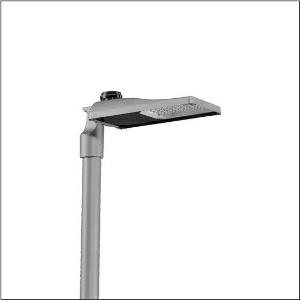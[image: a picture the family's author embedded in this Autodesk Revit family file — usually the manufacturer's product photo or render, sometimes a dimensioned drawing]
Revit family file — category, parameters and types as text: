
# Revit family: streetlight_sl_31_mini___st1_0a_5xh6d35n08ha_c5a6
name_source: partatom
category: Lighting Fixtures
units: mm (PartAtom-declared; Revit-internal decimal feet)

## family parameters
Cut with Voids When Loaded = No
Host = Face
Light Source = No
Part Type = Normal
Room Calculation Point = No
Round Connector Dimension = Use Diameter
Shared = No

## types (1)
- --- (1 x LED, 9240 lm, 68.3 W, 3000K)
    Apparent Load = 68 VA
    CIE Flux Codes = 37 72 97 100 100
    Color Rendering = 70
    Color Temperature = 3000K
    Default Elevation = 1800 mm
    Description = Streetlight SL 31 mini NEMA (7pin), Desk-Remote mast luminaire for post-top, side-entry; light control with lens of PMMA; light distribution: ST1.0a, direct asymmetric distribution, for standard-compliant lighting for roads and squares; LED: luminous flux: 9.240lm, light colour: 730, colour temperature: 3000K; luminous efficacy: 135,3lm/W; control: pre-setting: linear dimming characteristic, flexible luminous flux parameterisation, time-dependent luminous flux control, constant luminous flux control, intelligent temperature release in ECG and LED module, overheat protection; luminaire housing, of diecast aluminium, SITECO metallic grey (DB 702S), corrosivity category C5 high according to DIN EN ISO 12944; cover of toughened safety glass, transparent, opened without tools; mast flange of diecast aluminium, SITECO metallic grey (DB 702S), spigot size: 76/60mm, mast flange included unmounted; cable length: 8,5m, connection cable pre-assembled; mains connection: 220..240V, AC, 50/60Hz; power consumption (at start of service life): 68,3W / (at end of service life): 74,8W / (with reduced operation 50%): 29,7W; protection rating (complete): IP66; insulation class (complete): insulation class I (protective earthing); impact resistance: IK10; certification: CE, ENEC, ENEC+, VDE, UKCA; permissible operating ambient temperature for outdoor applications: -40..+50°C; packaging unit: 1 piece

Light Distribution: ST1.0a
    Height = 76 mm
    Lamp = 1 x LED
    Lamp Light Flux = 9240 lm
    Lamp Power = 68.3 W
    Lamp count = 1
    Length = 547 mm
    Luminous efficacy = 135 lm/W
    Manufacturer = Siteco
    ModVariant = No
    Model = 5XH6D35N08HA
    Number of Poles = 1
    OnlyDefault = Yes
    Power Factor = 1
    Product Name = Streetlight SL 31 mini | ST1.0a
    Product group = mast luminaire | pylon top
    ProductGroupID = 6100
    Protection Class = Protection class I
    Protection Degree = IP 66
    RLX_Detail_Level = 1
    RLX_Emergency_Light_Flux = 0 lm
    RLX_Emergency_Type = 0
    RLX_Emergency_Type_DB = No
    RlxData = <blob elided: 40129 chars, md5=6f445851>
    Socket = socket
    Standby Power = 0 W
    System Light Flux = 9240 lm
    System Power = 68 W
    Type Comments = factory setting: luminous flux: 100 % | dim-lin: 254 | 693 mA
    Type Image = l_1300322.jpg
    URL = http://relux.com
    VarID = @adj_060467
    Voltage = 0 V
    Weight = 0.00 kg
    Width = 265 mm

## geometry (parser evidence)
native form markers: Blend x4, Sweep x11
no freeform markers — native parametric forms only
